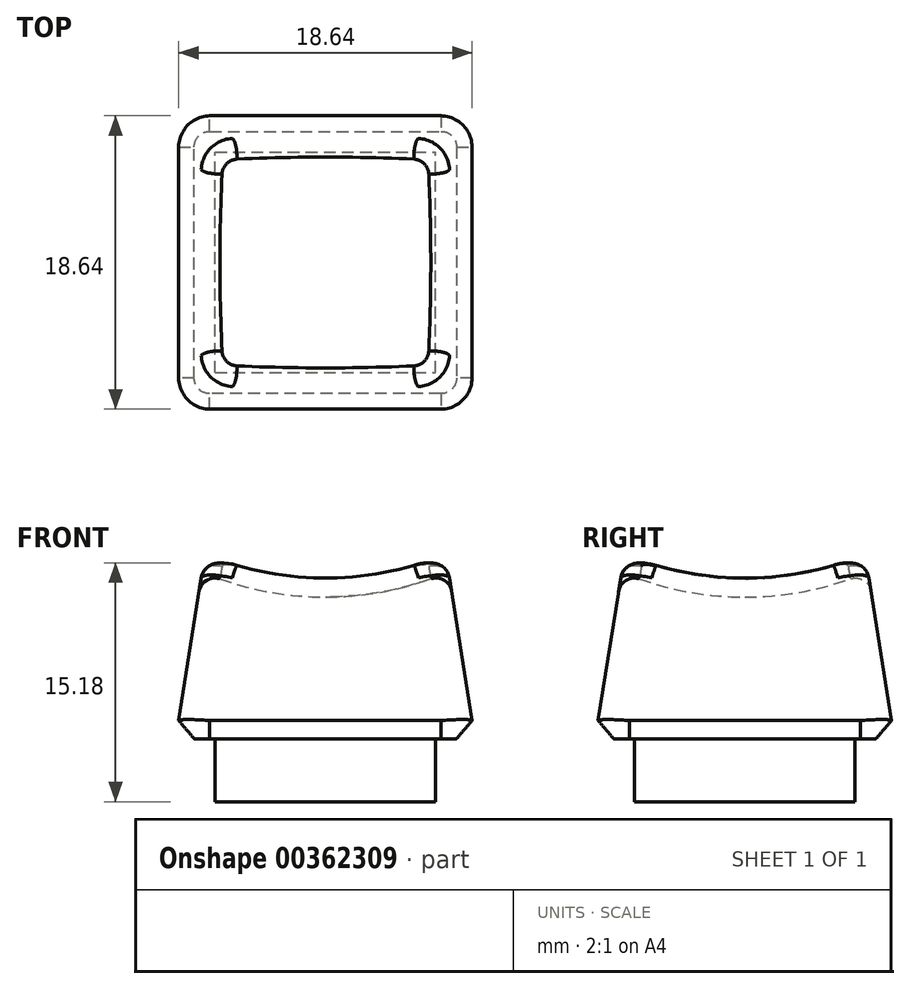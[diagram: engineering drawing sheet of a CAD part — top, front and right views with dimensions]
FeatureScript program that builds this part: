
annotation { "Feature Type Name" : "Feature", "Feature Type Description" : "" }
export const myFeature = defineFeature(function(context is Context, id is Id, definition is map)
    precondition{}
    {
        {
            var Q0;
            Q0=qCreatedBy(makeId("Top.planeOp"),FACE);
            var sketch = newSketch(context, id + "F0", { "sketchPlane" : qUnion([Q0])});
            skLineSegment(sketch, "E0.bottom", {"start": v(-9.5, 9.5) * mm, "end": v(9.5, 9.5) * mm});
            skLineSegment(sketch, "E0.top", {"start": v(-9.5, -9.5) * mm, "end": v(9.5, -9.5) * mm});
            skLineSegment(sketch, "E0.left", {"start": v(-9.5, 9.5) * mm, "end": v(-9.5, -9.5) * mm});
            skLineSegment(sketch, "E0.right", {"start": v(9.5, 9.5) * mm, "end": v(9.5, -9.5) * mm});
            skPoint(sketch, "E0.middle", {"position": v(0, 0) * mm});
            skSolve(sketch);
        }
        {
            var Q0;
            Q0 = qSketchRegion(id + "F0", true);
            extrude(context, id + "F1", {"entities" : qUnion([Q0]), "depth" : 12 * mm, "hasDraft" : true, "draftAngle" : 9 * degree, "draftPullDirection" : true});
        }
        {
            var Q0;
            Q0=makeQuery(id+"F1.opExtrude","SWEPT_EDGE",EDGE,{"disambiguationData":[OSD([sQuery(id+"F0.wireOp",EDGE,"E0.top"),sQuery(id+"F0.wireOp",EDGE,"E0.right")])]});
            var Q1;
            Q1=makeQuery(id+"F1.opExtrude","SWEPT_EDGE",EDGE,{"disambiguationData":[OSD([sQuery(id+"F0.wireOp",EDGE,"E0.top"),sQuery(id+"F0.wireOp",EDGE,"E0.left")])]});
            var Q2;
            Q2=makeQuery(id+"F1.opExtrude","SWEPT_EDGE",EDGE,{"disambiguationData":[OSD([sQuery(id+"F0.wireOp",EDGE,"E0.bottom"),sQuery(id+"F0.wireOp",EDGE,"E0.right")])]});
            var Q3;
            Q3=makeQuery(id+"F1.opExtrude","SWEPT_EDGE",EDGE,{"disambiguationData":[OSD([sQuery(id+"F0.wireOp",EDGE,"E0.bottom"),sQuery(id+"F0.wireOp",EDGE,"E0.left")])]});
            fillet(context, id + "F2", {"entities" : qUnion([Q0, Q1, Q2, Q3]), "radius" : 2 * mm, "tangentPropagation" : true, "allowEdgeOverflow" : false});
        }
        {
            var Q0;
            Q0=qCreatedBy(makeId("Front.planeOp"),FACE);
            var sketch = newSketch(context, id + "F3", { "sketchPlane" : qUnion([Q0])});
            skArc(sketch, "E1", {"start": v(0, 9) * mm, "mid": v(20, 29) * mm, "end": v(0, 49) * mm});
            skLineSegment(sketch, "E2", {"start": v(0, 49) * mm, "end": v(0, 9) * mm});
            skSolve(sketch);
        }
        {
            var Q0;
            Q0=makeQuery(id+"F3.imprint","IMPRINT",FACE,{"disambiguationData":[TD([[makeQuery(id+"F3.imprint","IMPRINT",EDGE,{"derivedFrom":sQuery(id+"F3.wireOp",EDGE,"E1")}),1.0]])]});
            var Q1;
            Q1=sQuery(id+"F3.wireOp",EDGE,"E2");
            revolve(context, id + "F4", {"operationType" : NewBodyOperationType.REMOVE, "entities" : qUnion([Q0]), "axis" : qUnion([Q1]), "revolveType" : RevolveType.FULL, "oppositeDirection" : true});
        }
        {
            var Q0;
            Q0=makeQuery(id+"F4.boolean.opBoolean","COPY",FACE,{"derivedFrom":makeQuery(id+"F4.opRevolve","SWEPT_FACE",FACE,{"disambiguationData":[OSD([sQuery(id+"F3.wireOp",EDGE,"E1")])]})});
            fillet(context, id + "F5", {"entities" : qUnion([Q0]), "radius" : 1 * mm, "tangentPropagation" : true, "allowEdgeOverflow" : false});
        }
        {
            var Q0;
            Q0=makeQuery(id+"F1.opExtrude","CAP_FACE",FACE,{"disambiguationData":[OSD([sQuery(id+"F0.wireOp",EDGE,"E0.bottom"),sQuery(id+"F0.wireOp",EDGE,"E0.top"),sQuery(id+"F0.wireOp",EDGE,"E0.left"),sQuery(id+"F0.wireOp",EDGE,"E0.right")])],"isStart":true});
            chamfer(context, id + "F6", {"entities" : qUnion([Q0]), "width" : 1 * mm, "tangentPropagation" : true});
        }
        {
            var Q0;
            Q0=makeQuery(id+"F1.opExtrude","CAP_FACE",FACE,{"disambiguationData":[OSD([sQuery(id+"F0.wireOp",EDGE,"E0.bottom"),sQuery(id+"F0.wireOp",EDGE,"E0.top"),sQuery(id+"F0.wireOp",EDGE,"E0.left"),sQuery(id+"F0.wireOp",EDGE,"E0.right")])],"isStart":true});
            var sketch = newSketch(context, id + "F7", { "sketchPlane" : qUnion([Q0])});
            skLineSegment(sketch, "E3.bottom", {"start": v(-7, 7) * mm, "end": v(7, 7) * mm});
            skLineSegment(sketch, "E3.top", {"start": v(-7, -7) * mm, "end": v(7, -7) * mm});
            skLineSegment(sketch, "E3.left", {"start": v(-7, 7) * mm, "end": v(-7, -7) * mm});
            skLineSegment(sketch, "E3.right", {"start": v(7, 7) * mm, "end": v(7, -7) * mm});
            skPoint(sketch, "E3.middle", {"position": v(0, 0) * mm});
            skSolve(sketch);
        }
        {
            var Q0;
            Q0 = qSketchRegion(id + "F7", true);
            extrude(context, id + "F8", {"entities" : qUnion([Q0]), "operationType" : NewBodyOperationType.ADD, "depth" : 4 * mm});
        }
    });
